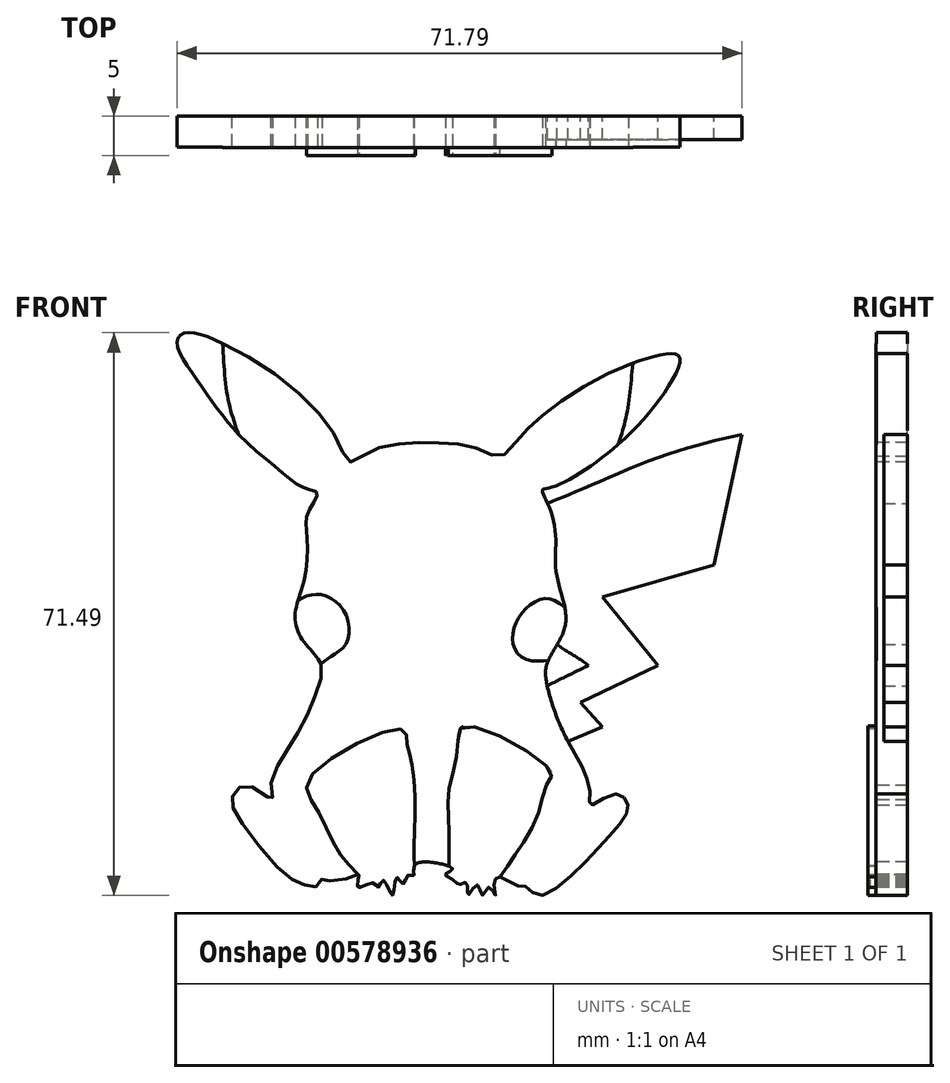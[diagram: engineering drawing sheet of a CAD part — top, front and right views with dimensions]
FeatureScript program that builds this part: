
annotation { "Feature Type Name" : "Feature", "Feature Type Description" : "" }
export const myFeature = defineFeature(function(context is Context, id is Id, definition is map)
    precondition{}
    {
        {
            var Q0;
            Q0=qCreatedBy(makeId("Front.planeOp"),FACE);
            var sketch = newSketch(context, id + "F0", { "sketchPlane" : qUnion([Q0])});
            skFitSpline(sketch, "E0", {"points": [v(-49.8, 55.06) * mm, v(-47.34, 56.3) * mm, v(-42.74, 57.42) * mm, v(-37.8, 57.42) * mm, v(-33.54, 56.75) * mm, v(-30.74, 55.74) * mm, v(-28.5, 57.87) * mm, v(-25.24, 61) * mm, v(-18.4, 65.6) * mm, v(-10.77, 68.52) * mm, v(-7.97, 68.41) * mm, v(-9.65, 64.15) * mm, v(-16.6, 56.52) * mm, v(-24.23, 51.81) * mm, v(-25.35, 51.47) * mm, v(-24.68, 49.8) * mm, v(-23.67, 45.64) * mm, v(-23.67, 41.72) * mm, v(-22.77, 37.67) * mm, v(-22.55, 33.87) * mm, v(-24.61, 29.83) * mm, v(-24.9, 27.47) * mm, v(-23.9, 23.66) * mm, v(-22.1, 19.51) * mm, v(-20.08, 15.8) * mm, v(-19.3, 12.56) * mm, v(-19.3, 11.44) * mm, v(-16.5, 12.78) * mm, v(-14.92, 12.33) * mm, v(-14.47, 10.87) * mm, v(-16.38, 8.07) * mm, v(-21.1, 3.02) * mm, v(-25.91, 0) * mm, v(-27.48, 1.12) * mm, v(-28.72, 1.23) * mm, v(-30.74, 2.35) * mm, v(-31.52, 1.34) * mm, v(-31.3, 0) * mm, v(-32.2, 1) * mm, v(-32.98, 0) * mm, v(-33.65, 1.34) * mm, v(-34.77, 0) * mm, v(-35, 1.57) * mm, v(-35.78, 1.34) * mm, v(-36.8, 2.01) * mm, v(-37.7, 2.69) * mm, v(-36.8, 3.25) * mm, v(-37.24, 3.7) * mm, v(-41.62, 3.8) * mm, v(-41.73, 2.46) * mm, v(-42.4, 2.57) * mm, v(-43.07, 1.45) * mm, v(-43.86, 2.24) * mm, v(-44.42, 0) * mm, v(-45.54, 1.9) * mm, v(-46.21, 1) * mm, v(-46.78, 1.57) * mm, v(-48.8, 1) * mm, v(-48.68, 2.57) * mm, v(-49.92, 2.24) * mm, v(-52.83, 1.9) * mm, v(-53.4, 2.01) * mm, v(-54.07, 1.12) * mm, v(-55.75, 1.34) * mm, v(-58.22, 2.8) * mm, v(-63.82, 9.64) * mm, v(-64.83, 12.1) * mm, v(-64.05, 13.57) * mm, v(-62.03, 13.68) * mm, v(-59.67, 12.1) * mm, v(-59.9, 13.57) * mm, v(-58.44, 17.38) * mm, v(-55.86, 21.64) * mm, v(-53.84, 26.35) * mm, v(-53.5, 29.38) * mm, v(-55.75, 32.3) * mm, v(-56.76, 35.77) * mm, v(-55.52, 40.48) * mm, v(-55.3, 45.98) * mm, v(-55.19, 48.45) * mm, v(-53.95, 51.03) * mm, v(-55.52, 51.7) * mm, v(-58.55, 53.83) * mm, v(-63.94, 58.54) * mm, v(-68.87, 64.93) * mm, v(-71.79, 70.2) * mm, v(-70.78, 71.4) * mm, v(-65.95, 70.1) * mm, v(-56.3, 63.81) * mm, v(-51.26, 57.53) * mm, v(-49.8, 55.06) * mm]});
            skFitSpline(sketch, "E1", {"points": [v(-48.68, 2.57) * mm, v(-51.4, 5.72) * mm, v(-54.06, 11.03) * mm, v(-54.96, 14.83) * mm, v(-43.24, 21.09) * mm, v(-42.59, 19.56) * mm, v(-42.11, 17.38) * mm, v(-41.5, 11.69) * mm, v(-41.7, 5.84) * mm, v(-41.62, 3.8) * mm], "startDerivative": vector(-26.96, 25.87) * mm, "endDerivative": vector(1.89, -23.72) * mm});
            skFitSpline(sketch, "E2", {"points": [v(-37.24, 3.7) * mm, v(-37.24, 4.85) * mm, v(-37.24, 8.94) * mm, v(-37.24, 13.27) * mm, v(-36.14, 18.64) * mm, v(-35.2, 21.48) * mm, v(-24.3, 15.8) * mm, v(-24.72, 14.21) * mm, v(-26, 10.05) * mm, v(-28.68, 5.33) * mm, v(-30.74, 2.35) * mm], "startDerivative": vector(-0.17, 18.18) * mm, "endDerivative": vector(-20.74, -30.02) * mm});
            skFitSpline(sketch, "E3", {"points": [v(-24.75, 26.6) * mm, v(-19.5, 29.2) * mm], "startDerivative": vector(5.16, 2.58) * mm, "endDerivative": vector(5.16, 2.58) * mm});
            skFitSpline(sketch, "E4", {"points": [v(-22.1, 19.51) * mm, v(-17.75, 21.38) * mm], "startDerivative": vector(4.36, 1.87) * mm, "endDerivative": vector(4.36, 1.87) * mm});
            skFitSpline(sketch, "E5", {"points": [v(-17.75, 21.38) * mm, v(-20.5, 24.52) * mm], "startDerivative": vector(-2.76, 3.14) * mm, "endDerivative": vector(-2.76, 3.14) * mm});
            skFitSpline(sketch, "E6", {"points": [v(-20.5, 24.52) * mm, v(-10.65, 29.2) * mm], "startDerivative": vector(9.86, 4.68) * mm, "endDerivative": vector(9.86, 4.68) * mm});
            skFitSpline(sketch, "E7", {"points": [v(-10.65, 29.2) * mm, v(-17.75, 37.86) * mm], "startDerivative": vector(-7.1, 8.66) * mm, "endDerivative": vector(-7.1, 8.66) * mm});
            skFitSpline(sketch, "E8", {"points": [v(-17.75, 37.86) * mm, v(-3.54, 41.97) * mm], "startDerivative": vector(14.21, 4.1) * mm, "endDerivative": vector(14.21, 4.1) * mm});
            skFitSpline(sketch, "E9", {"points": [v(-3.54, 41.97) * mm, v(0, 58.54) * mm], "startDerivative": vector(3.54, 16.57) * mm, "endDerivative": vector(3.54, 16.57) * mm});
            skFitSpline(sketch, "E10", {"points": [v(0, 58.54) * mm, v(-9.99, 55.84) * mm, v(-20.59, 51.47) * mm, v(-24.68, 49.8) * mm], "startDerivative": vector(-26.13, -5.91) * mm, "endDerivative": vector(-14.79, -5.87) * mm});
            skFitSpline(sketch, "E11", {"points": [v(-19.5, 29.2) * mm, v(-23.49, 31.84) * mm], "startDerivative": vector(-4, 3.06) * mm, "endDerivative": vector(-4, 3.06) * mm});
            skFitSpline(sketch, "E12", {"points": [v(-56.4, 37.47) * mm, v(-54.35, 38.22) * mm, v(-51.9, 37.54) * mm, v(-50.05, 34.9) * mm, v(-50.34, 31.87) * mm, v(-52.1, 30.4) * mm, v(-53.5, 29.38) * mm], "startDerivative": vector(12.6, 6.53) * mm, "endDerivative": vector(-9.4, -7.36) * mm});
            skFitSpline(sketch, "E13", {"points": [v(-24.61, 29.83) * mm, v(-26.91, 29.83) * mm, v(-28.7, 30.99) * mm, v(-29.13, 33.02) * mm, v(-28.38, 35.22) * mm, v(-26.63, 37.09) * mm, v(-24.61, 37.67) * mm, v(-22.52, 36.59) * mm], "startDerivative": vector(-13.6, -1.68) * mm, "endDerivative": vector(17.48, -11.8) * mm});
            skFitSpline(sketch, "E14", {"points": [v(-15.76, 57.24) * mm, v(-14.65, 61.1) * mm, v(-13.88, 67.6) * mm], "startDerivative": vector(2.81, 8.16) * mm, "endDerivative": vector(1.04, 12.36) * mm});
            skFitSpline(sketch, "E15", {"points": [v(-63.94, 58.54) * mm, v(-65.33, 63.2) * mm, v(-65.95, 70.1) * mm], "startDerivative": vector(-3.5, 9.64) * mm, "endDerivative": vector(-0.63, 13.35) * mm});
            skSolve(sketch);
        }
        {
            var Q0;
            {var subQ3=sQuery(id+"F0.wireOp",EDGE,"E2");Q0=makeQuery(id+"F0.imprint","IMPRINT",FACE,{"disambiguationData":[TD([[makeQuery(id+"F0.imprint","IMPRINT",EDGE,{"derivedFrom":subQ3}),1.0]])]});}
            extrude(context, id + "F1", {"entities" : qUnion([Q0]), "depth" : 4 * mm, "offsetDistance" : 25 * mm});
        }
        {
            var Q0;
            {var subQ0=sQuery(id+"F0.wireOp",EDGE,"E1");var subQ1=sQuery(id+"F0.wireOp",EDGE,"E0");var subQ2=makeQuery(id+"F0.imprint","INTERSECT",VERTEX,{"disambiguationData":[OD(0.0)],"derivedFrom":[subQ1,subQ0]});Q0=makeQuery(id+"F0.imprint","IMPRINT",FACE,{"disambiguationData":[TD([[makeQuery(id+"F0.imprint","IMPRINT",EDGE,{"disambiguationData":[TD([[subQ2,1.0]])],"derivedFrom":subQ1}),-1.0]])]});}
            var Q1;
            {var subQ0=sQuery(id+"F0.wireOp",EDGE,"E2");Q1=makeQuery(id+"F0.imprint","IMPRINT",FACE,{"disambiguationData":[TD([[makeQuery(id+"F0.imprint","IMPRINT",EDGE,{"derivedFrom":subQ0}),-1.0]])]});}
            extrude(context, id + "F2", {"entities" : qUnion([Q0, Q1]), "operationType" : NewBodyOperationType.ADD, "depth" : 5 * mm, "offsetDistance" : 25 * mm});
        }
        {
            var Q0;
            {var subQ3=sQuery(id+"F0.wireOp",EDGE,"E3");Q0=makeQuery(id+"F0.imprint","IMPRINT",FACE,{"disambiguationData":[TD([[makeQuery(id+"F0.imprint","IMPRINT",EDGE,{"derivedFrom":subQ3}),-1.0]])]});}
            extrude(context, id + "F3", {"entities" : qUnion([Q0]), "operationType" : NewBodyOperationType.ADD, "depth" : 3 * mm, "offsetDistance" : 25 * mm});
        }
        {
            var Q0;
            {var subQ0=sQuery(id+"F0.wireOp",EDGE,"E12");Q0=makeQuery(id+"F0.imprint","IMPRINT",FACE,{"disambiguationData":[TD([[makeQuery(id+"F0.imprint","IMPRINT",EDGE,{"derivedFrom":subQ0}),-1.0]])]});}
            var Q1;
            {var subQ0=sQuery(id+"F0.wireOp",EDGE,"E15");Q1=makeQuery(id+"F0.imprint","IMPRINT",FACE,{"disambiguationData":[TD([[makeQuery(id+"F0.imprint","IMPRINT",EDGE,{"derivedFrom":subQ0}),1.0]])]});}
            var Q2;
            {var subQ0=sQuery(id+"F0.wireOp",EDGE,"E14");Q2=makeQuery(id+"F0.imprint","IMPRINT",FACE,{"disambiguationData":[TD([[makeQuery(id+"F0.imprint","IMPRINT",EDGE,{"derivedFrom":subQ0}),-1.0]])]});}
            var Q3;
            {var subQ2=sQuery(id+"F0.wireOp",EDGE,"E13");Q3=makeQuery(id+"F0.imprint","IMPRINT",FACE,{"disambiguationData":[TD([[makeQuery(id+"F0.imprint","IMPRINT",EDGE,{"derivedFrom":subQ2}),-1.0]])]});}
            extrude(context, id + "F4", {"entities" : qUnion([Q0, Q1, Q2, Q3]), "operationType" : NewBodyOperationType.ADD, "depth" : 3.9 * mm, "offsetDistance" : 25 * mm});
        }
    });
